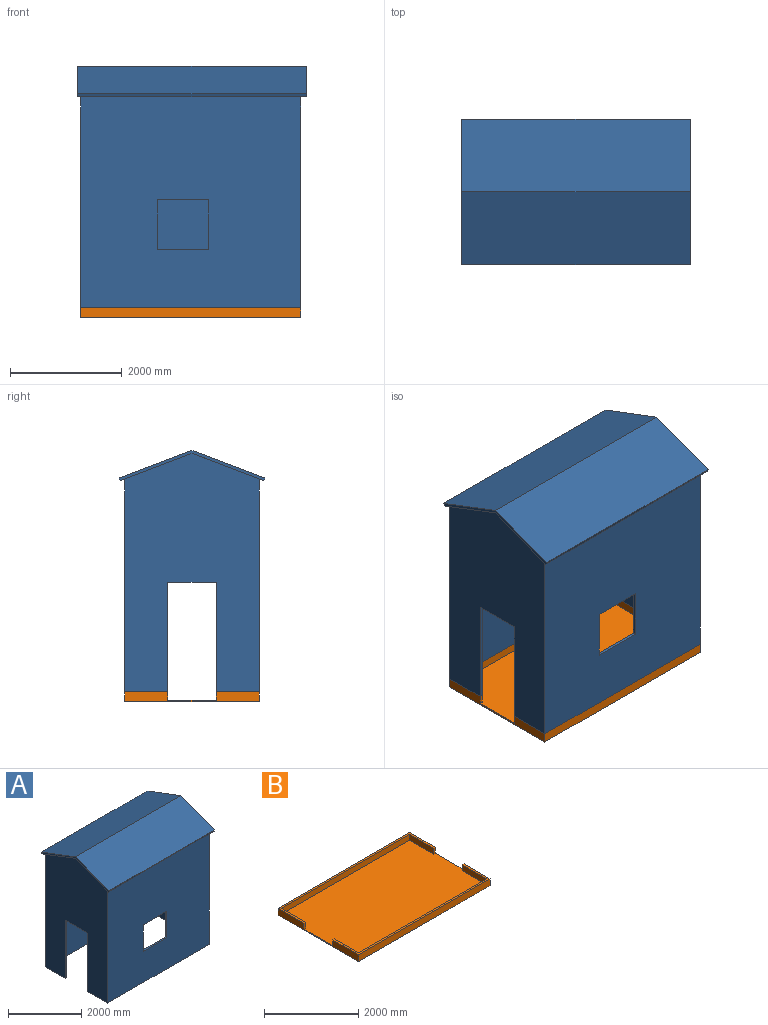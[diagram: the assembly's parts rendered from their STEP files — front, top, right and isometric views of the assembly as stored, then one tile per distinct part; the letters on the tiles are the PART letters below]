
ASSEMBLY  parts=2 mates=1
PART A: 30 faces, bbox 4089.4x2603x4318 mm
  f0: plane 4263.68x2413mm, normal (1,0,0), area 8047606.7mm2, adj f2,f3,f8,f13,f17,f18,f20,f21
  f1: plane 4263.68x2311.4mm, normal (1,0,0), area 7659890.9mm2, adj f2,f9,f12,f16,f18,f19,f23,f24
  f2: plane 3937x774.7mm, normal (0,0,-1), area 273547.8mm2, adj f0,f1,f10,f11,f12,f13,f21,f24
  f3: plane 4089.4x1283.51mm, normal (0,0.35,-0.94), area 533389.8mm2, adj f0,f4,f5,f6,f8,f10,f13
  f4: plane 2603.01x540.71mm, normal (-1,0,0), area 140431.2mm2, adj f3,f5,f7,f8,f14,f15
  f5: plane 4089.4x47.5mm, normal (0,-0.94,-0.35), area 207741.5mm2, adj f3,f4,f6,f7
  f6: plane 2603.01x540.71mm, normal (1,0,0), area 140431.2mm2, adj f3,f5,f7,f8,f14,f15
  f7: plane 4089.4x1301.51mm, normal (0,-0.35,0.94), area 5691718.9mm2, adj f4,f5,f6,f15
  f8: plane 4089.4x1283.51mm, normal (0,-0.35,-0.94), area 533389.8mm2, adj f0,f3,f4,f6,f10,f14,f17
  f9: plane 3835.4x1155.7mm, normal (0,-0.35,-0.94), area 4740160.7mm2, adj f1,f11,f16,f19
  f10: plane 4263.68x2413mm, normal (-1,0,0), area 8047606.7mm2, adj f2,f3,f8,f13,f17,f18,f23,f24
  f11: plane 4263.68x2311.4mm, normal (-1,0,0), area 7659890.9mm2, adj f2,f9,f12,f16,f18,f19,f20,f21
  f12: plane 3835.4x3825.73mm, normal (0,1,0), area 13860285.5mm2, adj f1,f2,f11,f19,f26,f27,f28,f29
  f13: plane 3937x3806.48mm, normal (0,-1,0), area 14173189.9mm2, adj f0,f2,f3,f10,f26,f27,f28,f29
  f14: plane 4089.4x47.5mm, normal (0,0.94,-0.35), area 207741.5mm2, adj f4,f6,f8,f15
  f15: plane 4089.4x1301.51mm, normal (0,0.35,0.94), area 5691718.9mm2, adj f4,f6,f7,f14
  f16: plane 3835.4x3825.73mm, normal (0,-1,0), area 14673187.1mm2, adj f1,f9,f11,f18
  f17: plane 3937x3806.48mm, normal (0,1,0), area 14986091.5mm2, adj f0,f8,f10,f18
  f18: plane 3937x774.7mm, normal (0,0,-1), area 273547.8mm2, adj f0,f1,f10,f11,f16,f17,f20,f23
  f19: plane 3835.4x1155.7mm, normal (0,0.35,-0.94), area 4740160.7mm2, adj f1,f9,f11,f12
  f20: plane 1955.8x50.8mm, normal (0,-1,0), area 99354.6mm2, adj f0,f11,f18,f22
  f21: plane 1955.8x50.8mm, normal (0,1,0), area 99354.6mm2, adj f0,f2,f11,f22
  f22: plane 863.6x50.8mm, normal (0,0,-1), area 43870.9mm2, adj f0,f11,f20,f21
  f23: plane 1955.8x50.8mm, normal (0,-1,0), area 99354.6mm2, adj f1,f10,f18,f25
  f24: plane 1955.8x50.8mm, normal (0,1,0), area 99354.6mm2, adj f1,f2,f10,f25
  f25: plane 863.6x50.8mm, normal (0,0,-1), area 43870.9mm2, adj f1,f10,f23,f24
  f26: plane 889x50.8mm, normal (1,0,0), area 45161.2mm2, adj f12,f13,f28,f29
  f27: plane 889x50.8mm, normal (-1,0,0), area 45161.2mm2, adj f12,f13,f28,f29
  f28: plane 914.4x50.8mm, normal (0,0,-1), area 46451.5mm2, adj f12,f13,f26,f27
  f29: plane 914.4x50.8mm, normal (0,0,1), area 46451.5mm2, adj f12,f13,f26,f27
PART B: 18 faces, bbox 3937x2413x177.8 mm
  f0: plane 723.9x152.4mm, normal (1,0,0), area 110322.4mm2, adj f9,f12,f13,f16
  f1: plane 723.9x152.4mm, normal (-1,0,0), area 110322.4mm2, adj f9,f12,f13,f14
  f2: plane 2413x177.8mm, normal (-1,0,0), area 297418.8mm2, adj f3,f5,f6,f7,f12,f13,f16,f17
  f3: plane 3937x774.7mm, normal (0,0,1), area 273547.8mm2, adj f2,f4,f6,f8,f10,f11,f15,f17
  f4: plane 2413x177.8mm, normal (1,0,0), area 297418.8mm2, adj f3,f5,f6,f7,f12,f13,f14,f15
  f5: plane 3937x177.8mm, normal (0,1,0), area 699998.6mm2, adj f2,f4,f7,f12
  f6: plane 3937x177.8mm, normal (0,-1,0), area 699998.6mm2, adj f2,f3,f4,f7
  f7: plane 3937x2413mm, normal (0,0,-1), area 9499981mm2, adj f2,f4,f5,f6
  f8: plane 723.9x152.4mm, normal (1,0,0), area 110322.4mm2, adj f3,f11,f13,f17
  f9: plane 3835.4x152.4mm, normal (0,-1,0), area 584515mm2, adj f0,f1,f12,f13
  f10: plane 723.9x152.4mm, normal (-1,0,0), area 110322.4mm2, adj f3,f11,f13,f15
  f11: plane 3835.4x152.4mm, normal (0,1,0), area 584515mm2, adj f3,f8,f10,f13
  f12: plane 3937x774.7mm, normal (0,0,1), area 273547.8mm2, adj f0,f1,f2,f4,f5,f9,f14,f16
  f13: plane 3937x2311.4mm, normal (0,0,1), area 8952885.3mm2, adj f0,f1,f2,f4,f8,f9,f10,f11
  f14: plane 152.4x50.8mm, normal (0,-1,0), area 7741.9mm2, adj f1,f4,f12,f13
  f15: plane 152.4x50.8mm, normal (0,1,0), area 7741.9mm2, adj f3,f4,f10,f13
  f16: plane 152.4x50.8mm, normal (0,-1,0), area 7741.9mm2, adj f0,f2,f12,f13
  f17: plane 152.4x50.8mm, normal (0,1,0), area 7741.9mm2, adj f2,f3,f8,f13
PLACE A at identity
PLACE B at identity
MATE fastened A.f2 <-> B.f3  axis (0,0,-1) through (1968.5,-1206.5,152.4)mm
